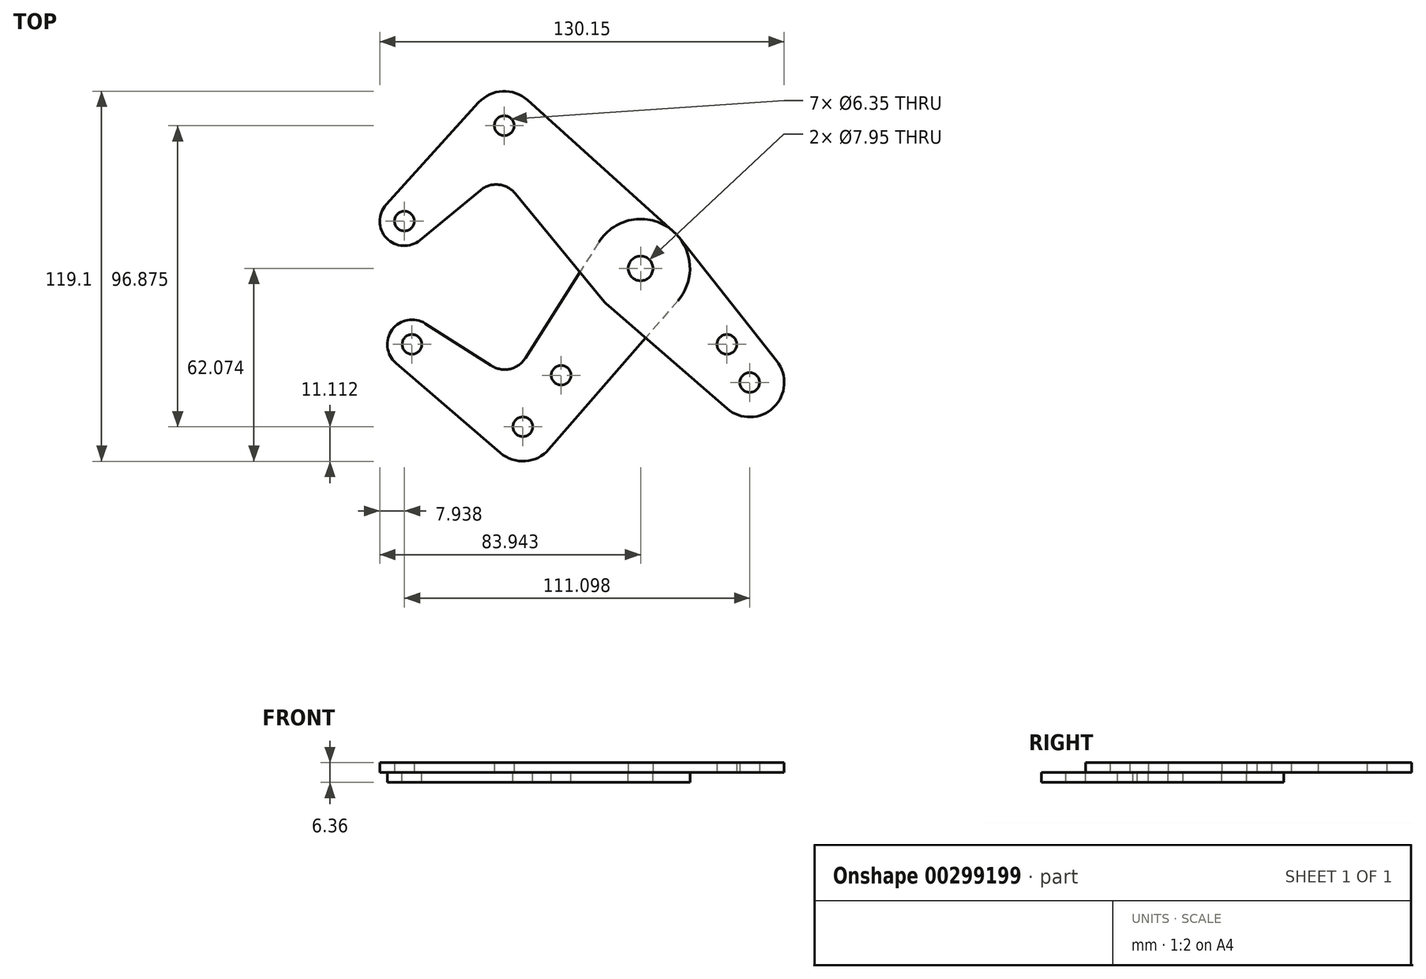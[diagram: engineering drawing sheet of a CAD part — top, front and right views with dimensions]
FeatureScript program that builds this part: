
annotation { "Feature Type Name" : "Feature", "Feature Type Description" : "" }
export const myFeature = defineFeature(function(context is Context, id is Id, definition is map)
    precondition{}
    {
        {
            var Q0;
            Q0=qCreatedBy(makeId("Top.planeOp"),FACE);
            var sketch = newSketch(context, id + "F0", { "sketchPlane" : qUnion([Q0])});
            skCircle(sketch, "E0", {"center": v(-38.12, 72.06) * mm, "radius": 7.94 * mm});
            skCircle(sketch, "E1", {"center": v(37.88, 56.85) * mm, "radius": 15.88 * mm});
            skCircle(sketch, "E2", {"center": v(72.98, 20.12) * mm, "radius": 11.11 * mm});
            skCircle(sketch, "E3", {"center": v(0, 5.9) * mm, "radius": 11.11 * mm});
            skCircle(sketch, "E4", {"center": v(65.65, 32.39) * mm, "radius": 3.18 * mm});
            skCircle(sketch, "E5", {"center": v(12.32, 22.47) * mm, "radius": 3.18 * mm});
            skCircle(sketch, "E6", {"center": v(-5.98, 102.77) * mm, "radius": 11.11 * mm});
            skLineSegment(sketch, "E7", {"start": v(49.88, 46.45) * mm, "end": v(8.4, -1.39) * mm});
            skLineSegment(sketch, "E8", {"start": v(-10.4, 107.4) * mm, "end": v(133.79, -43.53) * mm, "construction": true});
            skLineSegment(sketch, "E9", {"start": v(1.45, 111.02) * mm, "end": v(48.5, 68.65) * mm});
            skLineSegment(sketch, "E10", {"start": v(50.34, 66.7) * mm, "end": v(81.7, 27.01) * mm});
            skLineSegment(sketch, "E11", {"start": v(-5.98, 102.77) * mm, "end": v(-38.12, 72.06) * mm, "construction": true});
            skLineSegment(sketch, "E12", {"start": v(-44, 77.4) * mm, "end": v(-14.21, 110.23) * mm});
            skLineSegment(sketch, "E13", {"start": v(-33.06, 65.95) * mm, "end": v(-13.64, 82.01) * mm});
            skLineSegment(sketch, "E14", {"start": v(-14.57, 95.72) * mm, "end": v(-14.04, 95.07) * mm});
            skCircle(sketch, "E15", {"center": v(-35.67, 32.41) * mm, "radius": 7.94 * mm});
            skArc(sketch, "E16", {"start": v(-2.43, 80.93) * mm, "mid": v(-7.81, 83.8) * mm, "end": v(-13.64, 82.01) * mm});
            skLineSegment(sketch, "E17.trimOffspring", {"start": v(-2.43, 80.93) * mm, "end": v(25.61, 46.78) * mm});
            skLineSegment(sketch, "E18", {"start": v(27.48, 44.86) * mm, "end": v(65.7, 11.73) * mm});
            skLineSegment(sketch, "E19", {"start": v(37.88, 56.85) * mm, "end": v(0, 5.9) * mm, "construction": true});
            skLineSegment(sketch, "E20", {"start": v(-35.67, 32.41) * mm, "end": v(0, 5.9) * mm, "construction": true});
            skLineSegment(sketch, "E21", {"start": v(-40.85, 26.4) * mm, "end": v(-7.25, -2.53) * mm});
            skLineSegment(sketch, "E22", {"start": v(-31.4, 39.1) * mm, "end": v(-10.15, 25.55) * mm});
            skLineSegment(sketch, "E23", {"start": v(24.47, 65.34) * mm, "end": v(0.84, 28) * mm});
            skArc(sketch, "E24", {"start": v(-10.15, 25.55) * mm, "mid": v(-4.15, 24.5) * mm, "end": v(0.84, 28) * mm});
            skLineSegment(sketch, "E25.trimOffspring", {"start": v(-8.94, 12.54) * mm, "end": v(-9.4, 11.83) * mm});
            skLineSegment(sketch, "E26", {"start": v(-38.12, 72.06) * mm, "end": v(-35.67, 32.41) * mm, "construction": true});
            skCircle(sketch, "E27", {"center": v(0, 5.9) * mm, "radius": 3.18 * mm});
            skCircle(sketch, "E28", {"center": v(-35.67, 32.41) * mm, "radius": 3.18 * mm});
            skCircle(sketch, "E29", {"center": v(37.88, 56.85) * mm, "radius": 3.18 * mm});
            skCircle(sketch, "E30", {"center": v(37.88, 56.85) * mm, "radius": 3.98 * mm});
            skCircle(sketch, "E31", {"center": v(72.98, 20.12) * mm, "radius": 3.18 * mm});
            skCircle(sketch, "E32", {"center": v(-5.98, 102.77) * mm, "radius": 3.18 * mm});
            skCircle(sketch, "E33", {"center": v(-38.12, 72.06) * mm, "radius": 3.18 * mm});
            skSolve(sketch);
        }
        {
            var Q0;
            {var subQ7=sQuery(id+"F0.wireOp",EDGE,"E9");Q0=makeQuery(id+"F0.imprint","IMPRINT",FACE,{"disambiguationData":[TD([[makeQuery(id+"F0.imprint","IMPRINT",EDGE,{"derivedFrom":subQ7}),-1.0]])]});}
            var Q1;
            Q1=makeQuery(id+"F0.imprint","IMPRINT",FACE,{"disambiguationData":[TD([[makeQuery(id+"F0.imprint","IMPRINT",EDGE,{"derivedFrom":sQuery(id+"F0.wireOp",EDGE,"E33")}),-1.0]])]});
            var Q2;
            Q2=makeQuery(id+"F0.imprint","IMPRINT",FACE,{"disambiguationData":[TD([[makeQuery(id+"F0.imprint","IMPRINT",EDGE,{"derivedFrom":sQuery(id+"F0.wireOp",EDGE,"E32")}),-1.0]])]});
            var Q3;
            Q3=makeQuery(id+"F0.imprint","IMPRINT",FACE,{"disambiguationData":[TD([[makeQuery(id+"F0.imprint","IMPRINT",EDGE,{"derivedFrom":sQuery(id+"F0.wireOp",EDGE,"E30")}),-1.0]])]});
            var Q4;
            {var subQ0=sQuery(id+"F0.wireOp",EDGE,"E4");Q4=makeQuery(id+"F0.imprint","IMPRINT",FACE,{"disambiguationData":[TD([[makeQuery(id+"F0.imprint","IMPRINT",EDGE,{"derivedFrom":subQ0}),-1.0]])]});}
            var Q5;
            Q5=makeQuery(id+"F0.imprint","IMPRINT",FACE,{"disambiguationData":[TD([[makeQuery(id+"F0.imprint","IMPRINT",EDGE,{"derivedFrom":sQuery(id+"F0.wireOp",EDGE,"E31")}),-1.0]])]});
            var Q6;
            {var subQ0=sQuery(id+"F0.wireOp",EDGE,"E7");var subQ1=sQuery(id+"F0.wireOp",EDGE,"E1");var subQ2=makeQuery(id+"F0.imprint","INTERSECT",VERTEX,{"derivedFrom":[subQ1,subQ0]});Q6=makeQuery(id+"F0.imprint","IMPRINT",FACE,{"disambiguationData":[TD([[makeQuery(id+"F0.imprint","IMPRINT",EDGE,{"disambiguationData":[TD([[subQ2,1.0]])],"derivedFrom":subQ1}),-1.0]])]});}
            var Q7;
            {var subQ0=sQuery(id+"F0.wireOp",EDGE,"E17.trimOffspring");var subQ1=sQuery(id+"F0.wireOp",EDGE,"E1");var subQ2=makeQuery(id+"F0.imprint","INTERSECT",VERTEX,{"derivedFrom":[subQ1,subQ0]});Q7=makeQuery(id+"F0.imprint","IMPRINT",FACE,{"disambiguationData":[TD([[makeQuery(id+"F0.imprint","IMPRINT",EDGE,{"disambiguationData":[TD([[subQ2,1.0]])],"derivedFrom":subQ1}),-1.0]])]});}
            extrude(context, id + "F1", {"entities" : qUnion([Q0, Q1, Q2, Q3, Q4, Q5, Q6, Q7]), "depth" : 3.17 * mm});
        }
        {
            var Q0;
            Q0=makeQuery(id+"F0.imprint","IMPRINT",FACE,{"disambiguationData":[TD([[makeQuery(id+"F0.imprint","IMPRINT",EDGE,{"derivedFrom":sQuery(id+"F0.wireOp",EDGE,"E5")}),-1.0]])]});
            var Q1;
            Q1=makeQuery(id+"F0.imprint","IMPRINT",FACE,{"disambiguationData":[TD([[makeQuery(id+"F0.imprint","IMPRINT",EDGE,{"derivedFrom":sQuery(id+"F0.wireOp",EDGE,"E30")}),-1.0]])]});
            var Q2;
            {var subQ0=sQuery(id+"F0.wireOp",EDGE,"E17.trimOffspring");var subQ1=sQuery(id+"F0.wireOp",EDGE,"E1");var subQ2=makeQuery(id+"F0.imprint","INTERSECT",VERTEX,{"derivedFrom":[subQ1,subQ0]});Q2=makeQuery(id+"F0.imprint","IMPRINT",FACE,{"disambiguationData":[TD([[makeQuery(id+"F0.imprint","IMPRINT",EDGE,{"disambiguationData":[TD([[subQ2,1.0]])],"derivedFrom":subQ1}),-1.0]])]});}
            var Q3;
            {var subQ0=sQuery(id+"F0.wireOp",EDGE,"E7");var subQ1=sQuery(id+"F0.wireOp",EDGE,"E1");var subQ2=makeQuery(id+"F0.imprint","INTERSECT",VERTEX,{"derivedFrom":[subQ1,subQ0]});Q3=makeQuery(id+"F0.imprint","IMPRINT",FACE,{"disambiguationData":[TD([[makeQuery(id+"F0.imprint","IMPRINT",EDGE,{"disambiguationData":[TD([[subQ2,1.0]])],"derivedFrom":subQ1}),-1.0]])]});}
            var Q4;
            Q4=makeQuery(id+"F0.imprint","IMPRINT",FACE,{"disambiguationData":[TD([[makeQuery(id+"F0.imprint","IMPRINT",EDGE,{"derivedFrom":sQuery(id+"F0.wireOp",EDGE,"E27")}),-1.0]])]});
            var Q5;
            Q5=makeQuery(id+"F0.imprint","IMPRINT",FACE,{"disambiguationData":[TD([[makeQuery(id+"F0.imprint","IMPRINT",EDGE,{"derivedFrom":sQuery(id+"F0.wireOp",EDGE,"E28")}),-1.0]])]});
            extrude(context, id + "F2", {"entities" : qUnion([Q0, Q1, Q2, Q3, Q4, Q5]), "oppositeDirection" : true, "depth" : 3.17 * mm});
        }
        {
            var Q0;
            Q0=makeQuery(id+"F1.opExtrude","CAP_FACE",FACE,{"disambiguationData":[OSD([sQuery(id+"F0.wireOp",EDGE,"E0"),sQuery(id+"F0.wireOp",EDGE,"E1"),sQuery(id+"F0.wireOp",EDGE,"E2"),sQuery(id+"F0.wireOp",EDGE,"E4"),sQuery(id+"F0.wireOp",EDGE,"E6"),sQuery(id+"F0.wireOp",EDGE,"E9"),sQuery(id+"F0.wireOp",EDGE,"E10"),sQuery(id+"F0.wireOp",EDGE,"E12"),sQuery(id+"F0.wireOp",EDGE,"E13"),sQuery(id+"F0.wireOp",EDGE,"E16"),sQuery(id+"F0.wireOp",EDGE,"E17.trimOffspring"),sQuery(id+"F0.wireOp",EDGE,"E18"),sQuery(id+"F0.wireOp",EDGE,"E30"),sQuery(id+"F0.wireOp",EDGE,"E31"),sQuery(id+"F0.wireOp",EDGE,"E32"),sQuery(id+"F0.wireOp",EDGE,"E33")])],"isStart":false});
            var sketch = newSketch(context, id + "F3", { "sketchPlane" : qUnion([Q0])});
            skCircle(sketch, "E34", {"center": v(-5.98, 102.77) * mm, "radius": 3.98 * mm});
            skCircle(sketch, "E35", {"center": v(37.88, 56.85) * mm, "radius": 3.98 * mm});
            skCircle(sketch, "E36", {"center": v(72.98, 20.12) * mm, "radius": 11.11 * mm});
            skSolve(sketch);
        }
    });
